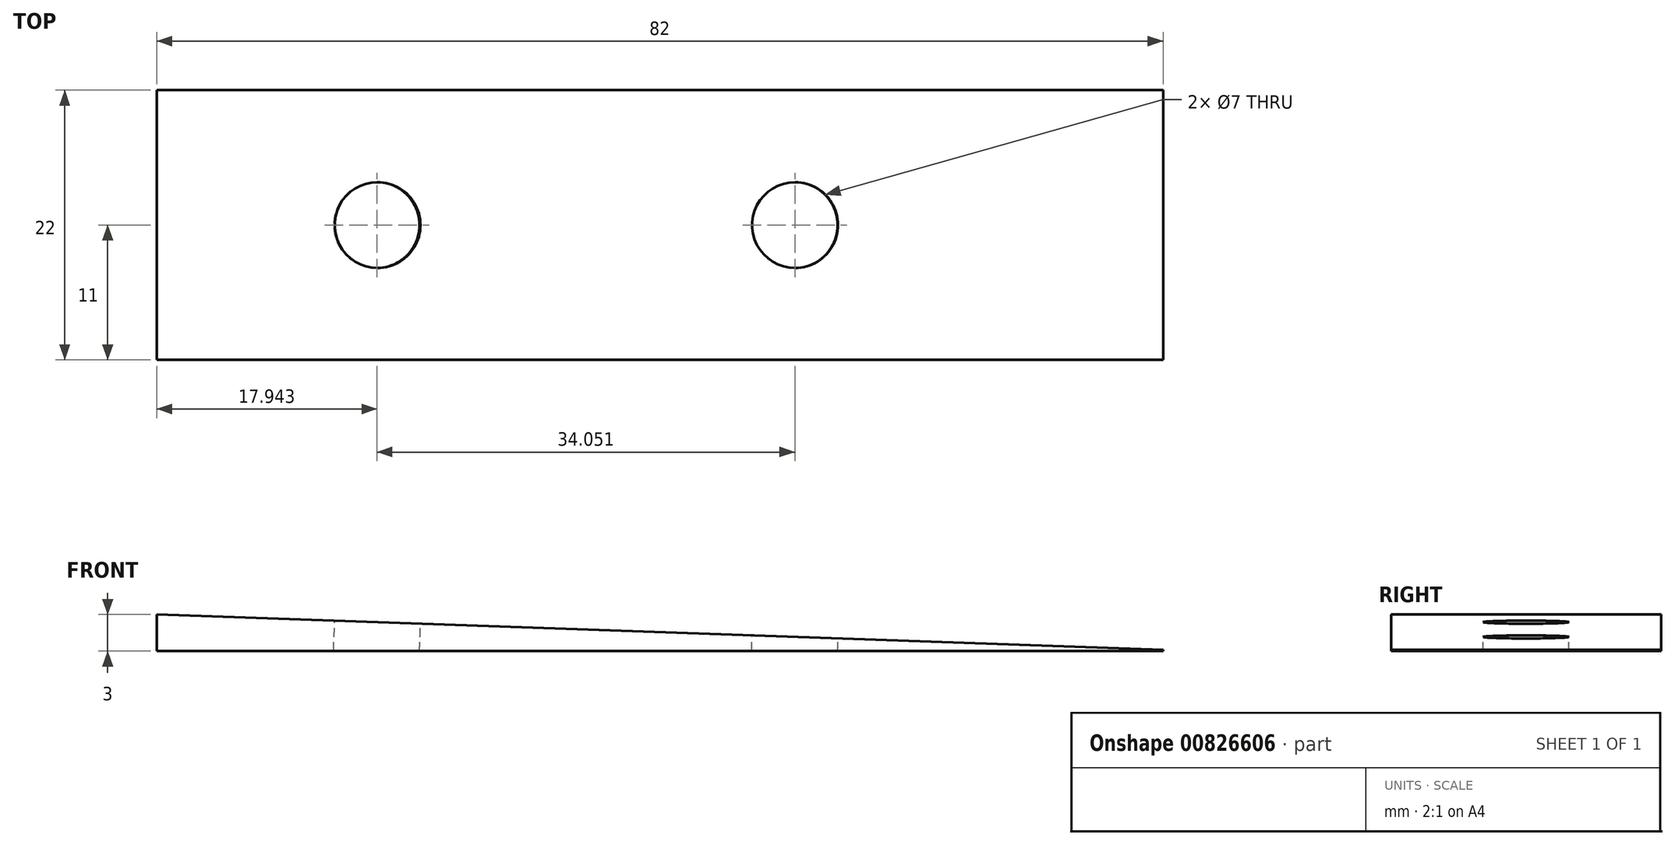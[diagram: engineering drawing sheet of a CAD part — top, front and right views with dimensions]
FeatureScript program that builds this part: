
annotation { "Feature Type Name" : "Feature", "Feature Type Description" : "" }
export const myFeature = defineFeature(function(context is Context, id is Id, definition is map)
    precondition{}
    {
        {
            var Q0;
            Q0=qCreatedBy(makeId("Front.planeOp"),FACE);
            var sketch = newSketch(context, id + "F0", { "sketchPlane" : qUnion([Q0])});
            skLineSegment(sketch, "E0", {"start": v(-30.94, 0) * mm, "end": v(51.06, 0) * mm});
            skLineSegment(sketch, "E1", {"start": v(-30.94, 0) * mm, "end": v(-30.94, 3) * mm});
            skLineSegment(sketch, "E2", {"start": v(51.06, 0) * mm, "end": v(51.06, 0.1) * mm});
            skLineSegment(sketch, "E3", {"start": v(51.06, 0.1) * mm, "end": v(-30.94, 3) * mm});
            skSolve(sketch);
        }
        {
            var Q0;
            Q0=makeQuery(id+"F0.imprint","IMPRINT",FACE,{"disambiguationData":[TD([[makeQuery(id+"F0.imprint","IMPRINT",EDGE,{"derivedFrom":sQuery(id+"F0.wireOp",EDGE,"E0")}),1.0]])]});
            extrude(context, id + "F1", {"entities" : qUnion([Q0]), "depth" : 22 * mm, "offsetDistance" : 25 * mm});
        }
        {
            var Q0;
            Q0=makeQuery(id+"F1.opExtrude","SWEPT_FACE",FACE,{"disambiguationData":[OSD([sQuery(id+"F0.wireOp",EDGE,"E3")])]});
            var sketch = newSketch(context, id + "F2", { "sketchPlane" : qUnion([Q0])});
            skPoint(sketch, "E4", {"position": v(-13.03, -11) * mm});
            skPoint(sketch, "E5", {"position": v(21.02, -11) * mm});
            skSolve(sketch);
        }
        {
            var Q0;
            Q0=sQuery(id+"F2.wireOp",VERTEX,"E4");
            var Q1;
            Q1=sQuery(id+"F2.wireOp",VERTEX,"E5");
            var Q2;
            Q2=makeQuery(id+"F1.opExtrude","SWEPT_BODY",BODY,{"disambiguationData":[OSD([sQuery(id+"F0.wireOp",EDGE,"E0"),sQuery(id+"F0.wireOp",EDGE,"E1"),sQuery(id+"F0.wireOp",EDGE,"E2"),sQuery(id+"F0.wireOp",EDGE,"E3")])]});
            hole(context, id + "F3", {"style" : HoleStyle.SIMPLE, "endStyle" : HoleEndStyle.BLIND, "holeDiameter" : 7 * mm, "majorDiameter" : 5 * mm, "holeDepth" : 14.4 * mm, "isTappedThrough" : true, "tappedDepth" : 12 * mm, "tapClearance" : 3, "locations" : qUnion([Q0, Q1]), "scope" : qUnion([Q2])});
        }
    });
